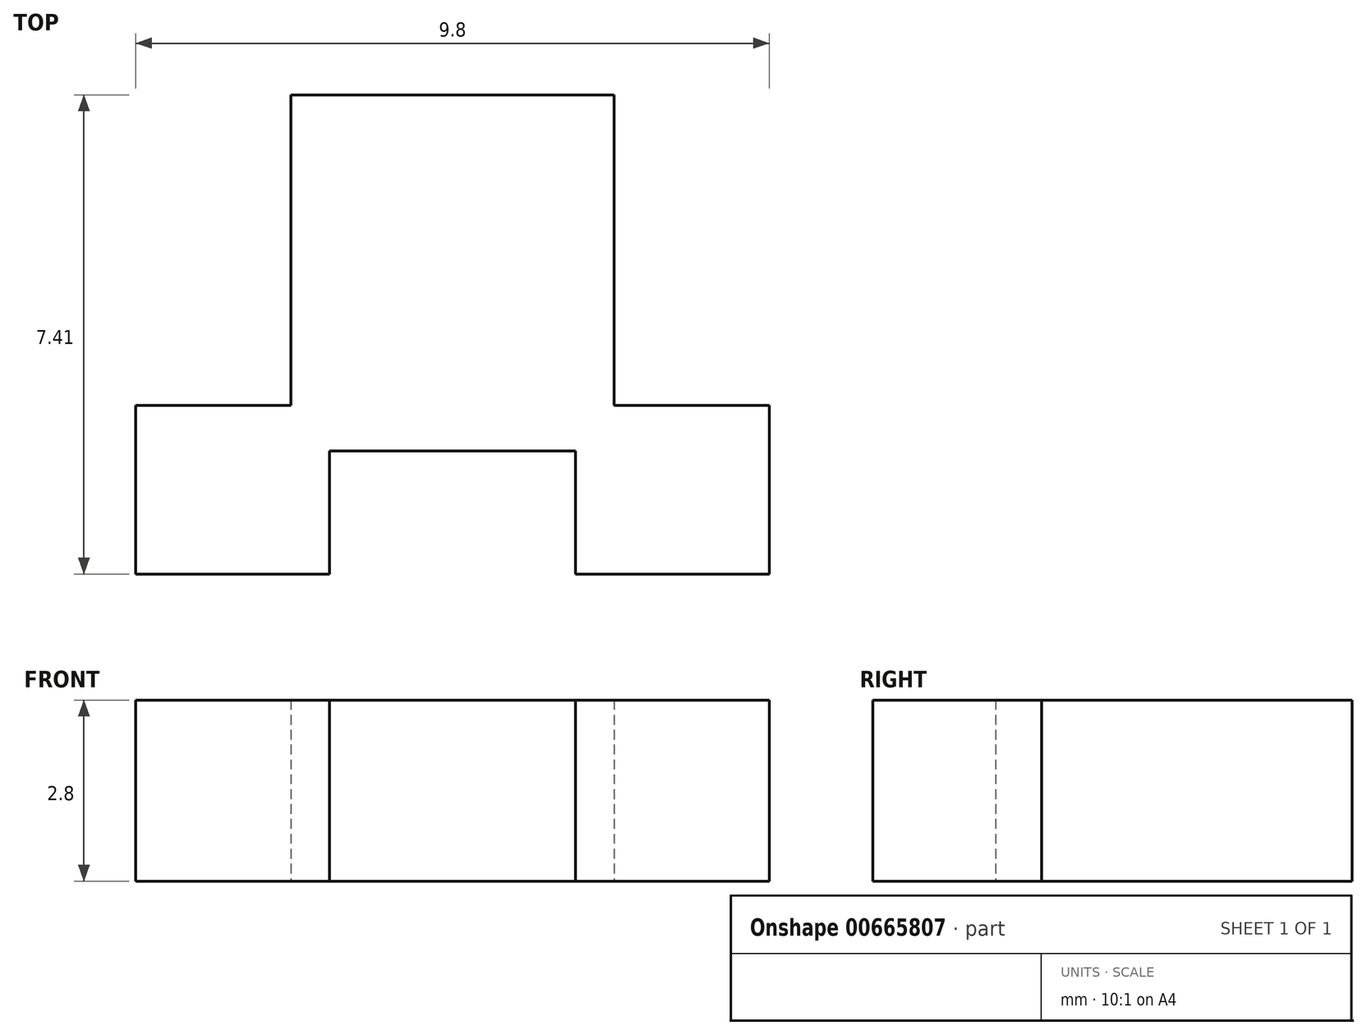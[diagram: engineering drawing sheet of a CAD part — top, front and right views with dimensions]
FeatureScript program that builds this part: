
annotation { "Feature Type Name" : "Feature", "Feature Type Description" : "" }
export const myFeature = defineFeature(function(context is Context, id is Id, definition is map)
    precondition{}
    {
        {
            var Q0;
            Q0=qCreatedBy(makeId("Top.planeOp"),FACE);
            var sketch = newSketch(context, id + "F0", { "sketchPlane" : qUnion([Q0])});
            skLineSegment(sketch, "E0.bottom", {"start": v(-2.5, 5.5) * mm, "end": v(2.5, 5.5) * mm});
            skLineSegment(sketch, "E0.top", {"start": v(-2.5, 0) * mm, "end": v(2.5, 0) * mm});
            skLineSegment(sketch, "E0.left", {"start": v(-2.5, 5.5) * mm, "end": v(-2.5, 0) * mm});
            skLineSegment(sketch, "E1.bottom", {"start": v(-4.9, 0.7) * mm, "end": v(-1.9, 0.7) * mm});
            skLineSegment(sketch, "E1.top", {"start": v(-4.9, -1.9) * mm, "end": v(-1.9, -1.9) * mm});
            skLineSegment(sketch, "E1.left", {"start": v(-4.9, 0.7) * mm, "end": v(-4.9, -1.9) * mm});
            skLineSegment(sketch, "E1.right", {"start": v(-1.9, 0.7) * mm, "end": v(-1.9, -1.9) * mm});
            skLineSegment(sketch, "E2.MirrorCS", {"start": v(1.9, 0.7) * mm, "end": v(1.9, -1.9) * mm});
            skLineSegment(sketch, "E3.MirrorCS", {"start": v(4.9, -1.9) * mm, "end": v(1.9, -1.9) * mm});
            skLineSegment(sketch, "E4.MirrorCS", {"start": v(4.9, 0.7) * mm, "end": v(1.9, 0.7) * mm});
            skLineSegment(sketch, "E5.MirrorCS", {"start": v(4.9, 0.7) * mm, "end": v(4.9, -1.9) * mm});
            skLineSegment(sketch, "E6.MirrorCS", {"start": v(2.5, 5.5) * mm, "end": v(2.5, 0) * mm});
            skSolve(sketch);
        }
        {
            var Q0;
            Q0 = qSketchRegion(id + "F0", true);
            extrude(context, id + "F1", {"entities" : qUnion([Q0]), "depth" : 2.8 * mm, "offsetDistance" : 25 * mm});
        }
    });
